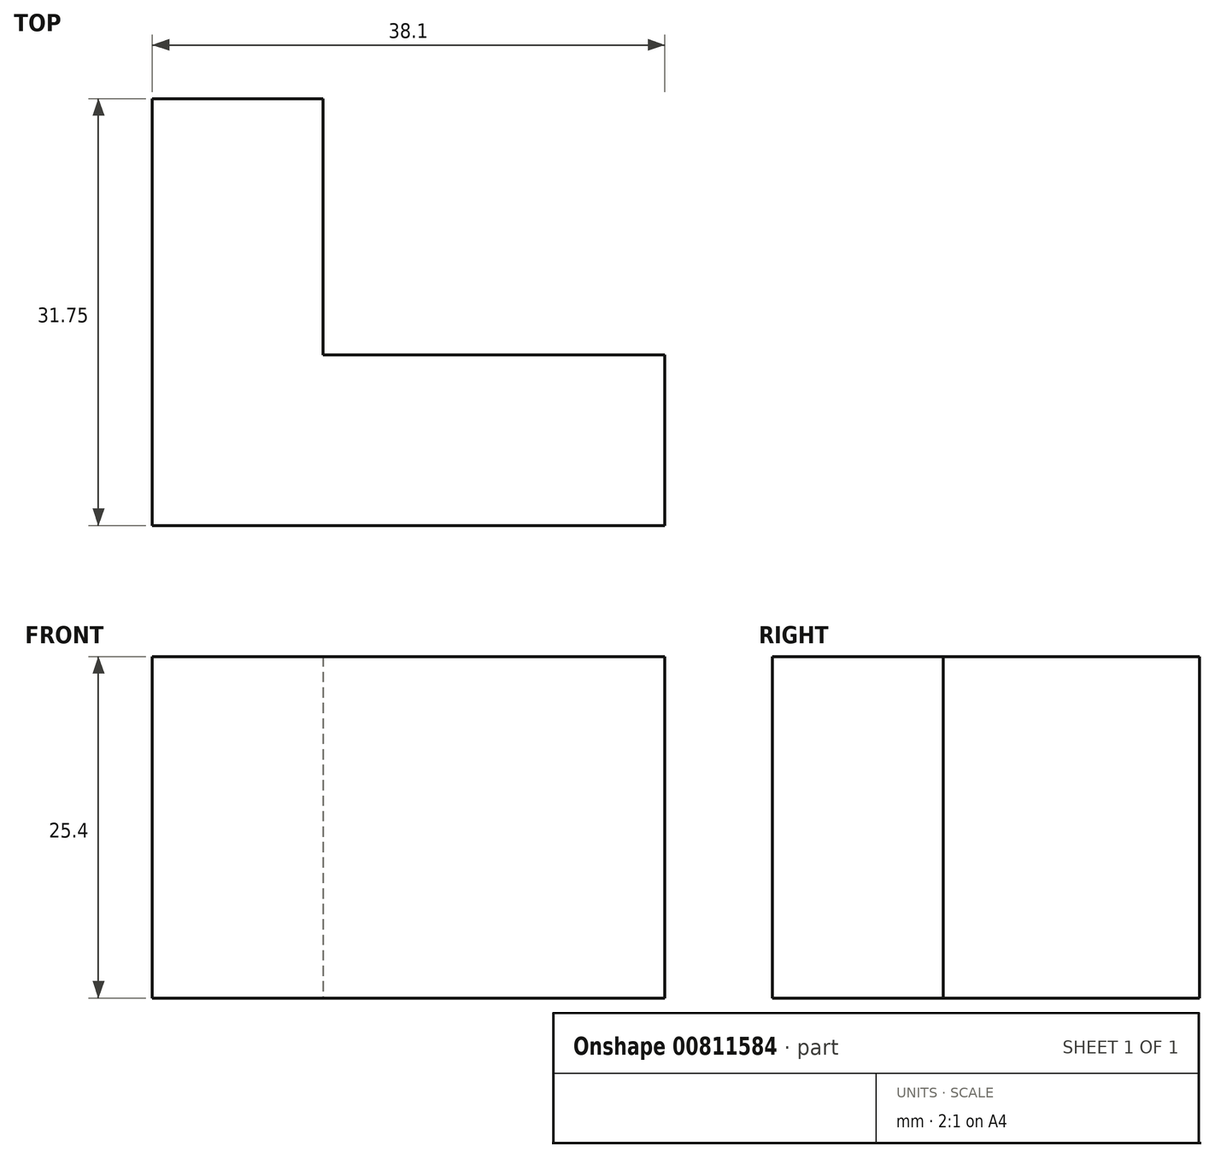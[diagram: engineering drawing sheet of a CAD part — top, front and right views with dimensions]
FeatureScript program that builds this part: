
annotation { "Feature Type Name" : "Feature", "Feature Type Description" : "" }
export const myFeature = defineFeature(function(context is Context, id is Id, definition is map)
    precondition{}
    {
        {
            var Q0;
            Q0=qCreatedBy(makeId("Top.planeOp"),FACE);
            var sketch = newSketch(context, id + "F0", { "sketchPlane" : qUnion([Q0])});
            skLineSegment(sketch, "E0", {"start": v(-55.97, 0) * mm, "end": v(-55.97, 31.75) * mm});
            skLineSegment(sketch, "E1", {"start": v(-55.97, 0) * mm, "end": v(-17.87, 0) * mm});
            skLineSegment(sketch, "E2", {"start": v(-17.87, 0) * mm, "end": v(-17.87, 12.7) * mm});
            skLineSegment(sketch, "E3", {"start": v(-17.87, 12.7) * mm, "end": v(-43.27, 12.7) * mm});
            skLineSegment(sketch, "E4", {"start": v(-43.27, 12.7) * mm, "end": v(-43.27, 31.75) * mm});
            skLineSegment(sketch, "E5", {"start": v(-55.97, 31.75) * mm, "end": v(-43.27, 31.75) * mm});
            skSolve(sketch);
        }
        {
            var Q0;
            Q0=makeQuery(id+"F0.imprint","IMPRINT",FACE,{"disambiguationData":[TD([[makeQuery(id+"F0.imprint","IMPRINT",EDGE,{"derivedFrom":sQuery(id+"F0.wireOp",EDGE,"E0")}),-1.0]])]});
            extrude(context, id + "F1", {"entities" : qUnion([Q0]), "depth" : 25.4 * mm, "offsetDistance" : 25.4 * mm});
        }
    });
